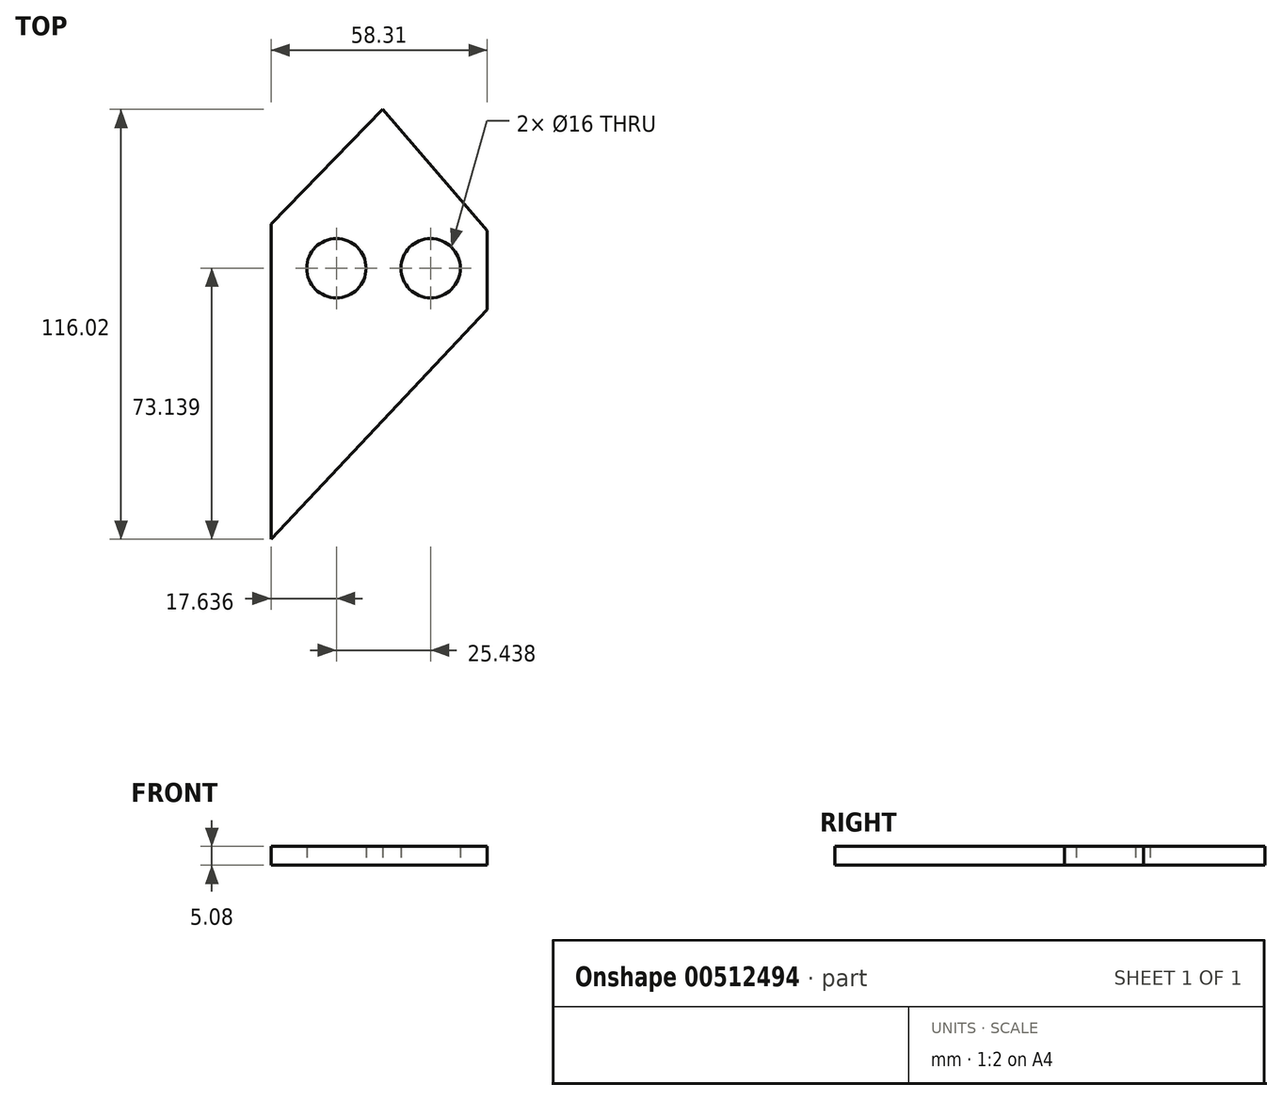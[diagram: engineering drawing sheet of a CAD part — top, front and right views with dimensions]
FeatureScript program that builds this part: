
annotation { "Feature Type Name" : "Feature", "Feature Type Description" : "" }
export const myFeature = defineFeature(function(context is Context, id is Id, definition is map)
    precondition{}
    {
        {
            var Q0;
            Q0=qCreatedBy(makeId("Top.planeOp"),FACE);
            var sketch = newSketch(context, id + "F0", { "sketchPlane" : qUnion([Q0])});
            skLineSegment(sketch, "E0.left", {"start": v(-27.25, -124.12) * mm, "end": v(-27.25, -102.78) * mm});
            skLineSegment(sketch, "E0.right", {"start": v(-85.56, -122.33) * mm, "end": v(-85.56, -101) * mm});
            skLineSegment(sketch, "E1", {"start": v(-85.56, -101) * mm, "end": v(-55.43, -70.06) * mm});
            skLineSegment(sketch, "E2", {"start": v(-55.43, -70.06) * mm, "end": v(-27.25, -102.78) * mm});
            skLineSegment(sketch, "E3", {"start": v(-27.25, -124.12) * mm, "end": v(-85.56, -186.08) * mm});
            skLineSegment(sketch, "E4", {"start": v(-85.56, -186.08) * mm, "end": v(-85.56, -122.33) * mm});
            skCircle(sketch, "E5", {"center": v(-42.49, -112.94) * mm, "radius": 8 * mm});
            skCircle(sketch, "E6", {"center": v(-67.92, -112.94) * mm, "radius": 8 * mm});
            skSolve(sketch);
        }
        {
            var Q0;
            Q0=makeQuery(id+"F0.imprint","IMPRINT",FACE,{"disambiguationData":[TD([[makeQuery(id+"F0.imprint","IMPRINT",EDGE,{"derivedFrom":sQuery(id+"F0.wireOp",EDGE,"E0.left")}),1.0]])]});
            extrude(context, id + "F1", {"entities" : qUnion([Q0]), "depth" : 5.08 * mm});
        }
    });
